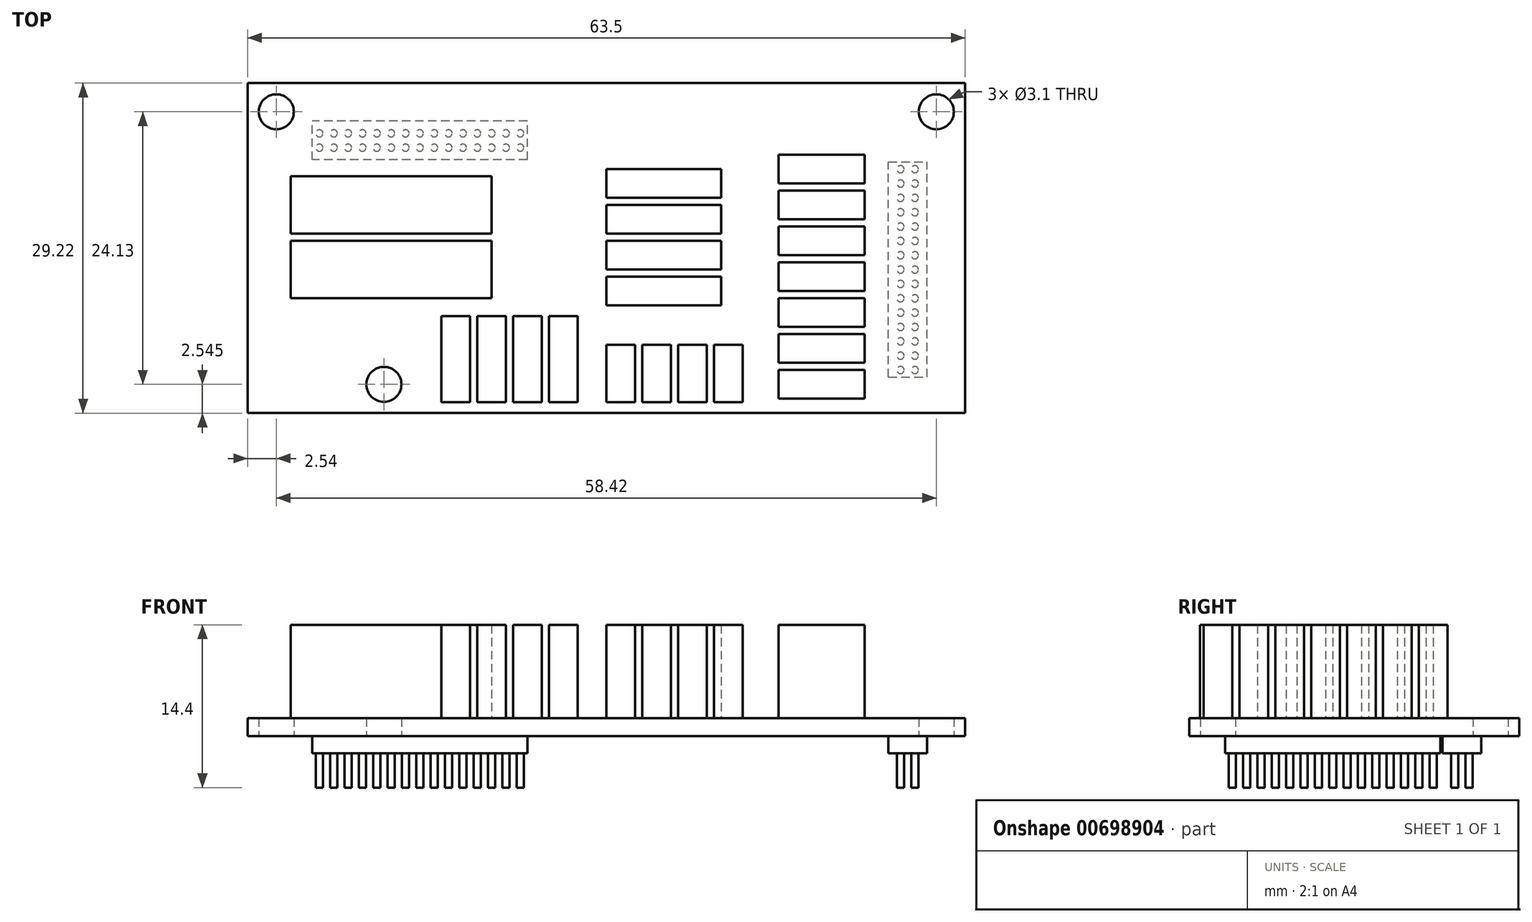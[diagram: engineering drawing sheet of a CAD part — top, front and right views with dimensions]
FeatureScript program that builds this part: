
annotation { "Feature Type Name" : "Feature", "Feature Type Description" : "" }
export const myFeature = defineFeature(function(context is Context, id is Id, definition is map)
    precondition{}
    {
        {
            var Q0;
            Q0=qCreatedBy(makeId("Top.planeOp"),FACE);
            var sketch = newSketch(context, id + "F0", { "sketchPlane" : qUnion([Q0])});
            skLineSegment(sketch, "E0.bottom", {"start": v(31.75, 14.6) * mm, "end": v(-31.75, 14.6) * mm});
            skLineSegment(sketch, "E0.top", {"start": v(31.75, -14.6) * mm, "end": v(-31.75, -14.6) * mm});
            skLineSegment(sketch, "E0.left", {"start": v(31.75, 14.6) * mm, "end": v(31.75, -14.6) * mm});
            skLineSegment(sketch, "E0.right", {"start": v(-31.75, 14.6) * mm, "end": v(-31.75, -14.6) * mm});
            skPoint(sketch, "E0.middle", {"position": v(0, 0) * mm});
            skCircle(sketch, "E1", {"center": v(-29.2, 12.07) * mm, "radius": 1.55 * mm});
            skCircle(sketch, "E2", {"center": v(29.21, 12.07) * mm, "radius": 1.55 * mm});
            skCircle(sketch, "E3", {"center": v(-19.69, -12.06) * mm, "radius": 1.55 * mm});
            skCircle(sketch, "E4", {"center": v(-25.4, 10.16) * mm, "radius": 0.32 * mm});
            skLineSegment(sketch, "E5", {"start": v(-29.2, 12.07) * mm, "end": v(29.21, 12.07) * mm, "construction": true});
            skCircle(sketch, "E6.1.0.0", {"center": v(-24.13, 10.16) * mm, "radius": 0.32 * mm});
            skCircle(sketch, "E6.2.0.0", {"center": v(-22.86, 10.16) * mm, "radius": 0.32 * mm});
            skCircle(sketch, "E6.3.0.0", {"center": v(-21.6, 10.16) * mm, "radius": 0.32 * mm});
            skCircle(sketch, "E6.4.0.0", {"center": v(-20.32, 10.16) * mm, "radius": 0.32 * mm});
            skCircle(sketch, "E6.5.0.0", {"center": v(-19.05, 10.16) * mm, "radius": 0.32 * mm});
            skCircle(sketch, "E6.6.0.0", {"center": v(-17.78, 10.16) * mm, "radius": 0.32 * mm});
            skCircle(sketch, "E6.7.0.0", {"center": v(-16.51, 10.16) * mm, "radius": 0.32 * mm});
            skCircle(sketch, "E6.8.0.0", {"center": v(-15.24, 10.16) * mm, "radius": 0.32 * mm});
            skCircle(sketch, "E6.9.0.0", {"center": v(-13.97, 10.16) * mm, "radius": 0.32 * mm});
            skCircle(sketch, "E6.10.0.0", {"center": v(-12.7, 10.16) * mm, "radius": 0.32 * mm});
            skCircle(sketch, "E6.11.0.0", {"center": v(-11.43, 10.16) * mm, "radius": 0.32 * mm});
            skCircle(sketch, "E6.12.0.0", {"center": v(-10.16, 10.16) * mm, "radius": 0.32 * mm});
            skCircle(sketch, "E6.13.0.0", {"center": v(-8.9, 10.16) * mm, "radius": 0.32 * mm});
            skCircle(sketch, "E6.14.0.0", {"center": v(-7.62, 10.16) * mm, "radius": 0.32 * mm});
            skLineSegment(sketch, "E6.direction1", {"start": v(-25.4, 10.16) * mm, "end": v(-24.13, 10.16) * mm, "construction": true});
            skCircle(sketch, "E7.1.0.0", {"center": v(-19.05, 8.89) * mm, "radius": 0.32 * mm});
            skCircle(sketch, "E7.1.0.1", {"center": v(-17.78, 8.89) * mm, "radius": 0.32 * mm});
            skCircle(sketch, "E7.1.0.2", {"center": v(-16.51, 8.89) * mm, "radius": 0.32 * mm});
            skCircle(sketch, "E7.1.0.3", {"center": v(-13.97, 8.89) * mm, "radius": 0.32 * mm});
            skCircle(sketch, "E7.1.0.4", {"center": v(-11.43, 8.89) * mm, "radius": 0.32 * mm});
            skCircle(sketch, "E7.1.0.5", {"center": v(-8.9, 8.89) * mm, "radius": 0.32 * mm});
            skCircle(sketch, "E7.1.0.6", {"center": v(-25.4, 8.9) * mm, "radius": 0.32 * mm});
            skCircle(sketch, "E7.1.0.7", {"center": v(-24.13, 8.9) * mm, "radius": 0.32 * mm});
            skCircle(sketch, "E7.1.0.8", {"center": v(-22.86, 8.89) * mm, "radius": 0.32 * mm});
            skCircle(sketch, "E7.1.0.9", {"center": v(-21.6, 8.89) * mm, "radius": 0.32 * mm});
            skCircle(sketch, "E7.1.0.10", {"center": v(-20.32, 8.89) * mm, "radius": 0.32 * mm});
            skLineSegment(sketch, "E7.1.0.11", {"start": v(-25.4, 8.9) * mm, "end": v(-24.13, 8.9) * mm, "construction": true});
            skCircle(sketch, "E7.1.0.12", {"center": v(-7.62, 8.89) * mm, "radius": 0.32 * mm});
            skCircle(sketch, "E7.1.0.13", {"center": v(-10.16, 8.89) * mm, "radius": 0.32 * mm});
            skCircle(sketch, "E7.1.0.14", {"center": v(-12.7, 8.89) * mm, "radius": 0.32 * mm});
            skCircle(sketch, "E7.1.0.15", {"center": v(-15.24, 8.89) * mm, "radius": 0.32 * mm});
            skLineSegment(sketch, "E7.direction1", {"start": v(-25.4, 10.16) * mm, "end": v(-25.4, 8.9) * mm, "construction": true});
            skCircle(sketch, "E8", {"center": v(-29.2, 12.07) * mm, "radius": 2.5 * mm, "construction": true});
            skCircle(sketch, "E9", {"center": v(27.3, 6.99) * mm, "radius": 0.32 * mm});
            skCircle(sketch, "E10.1.0.0", {"center": v(27.3, 5.72) * mm, "radius": 0.32 * mm});
            skCircle(sketch, "E10.2.0.0", {"center": v(27.3, 4.45) * mm, "radius": 0.32 * mm});
            skCircle(sketch, "E10.3.0.0", {"center": v(27.3, 3.18) * mm, "radius": 0.32 * mm});
            skCircle(sketch, "E10.4.0.0", {"center": v(27.3, 1.9) * mm, "radius": 0.32 * mm});
            skCircle(sketch, "E10.5.0.0", {"center": v(27.3, 0.64) * mm, "radius": 0.32 * mm});
            skCircle(sketch, "E10.6.0.0", {"center": v(27.3, -0.63) * mm, "radius": 0.32 * mm});
            skCircle(sketch, "E10.7.0.0", {"center": v(27.3, -1.9) * mm, "radius": 0.32 * mm});
            skCircle(sketch, "E10.8.0.0", {"center": v(27.3, -3.17) * mm, "radius": 0.32 * mm});
            skCircle(sketch, "E10.9.0.0", {"center": v(27.3, -4.44) * mm, "radius": 0.32 * mm});
            skCircle(sketch, "E10.10.0.0", {"center": v(27.3, -5.71) * mm, "radius": 0.32 * mm});
            skCircle(sketch, "E10.11.0.0", {"center": v(27.3, -6.98) * mm, "radius": 0.32 * mm});
            skCircle(sketch, "E10.12.0.0", {"center": v(27.3, -8.25) * mm, "radius": 0.32 * mm});
            skCircle(sketch, "E10.13.0.0", {"center": v(27.3, -9.52) * mm, "radius": 0.32 * mm});
            skCircle(sketch, "E10.14.0.0", {"center": v(27.3, -10.8) * mm, "radius": 0.32 * mm});
            skLineSegment(sketch, "E10.direction1", {"start": v(27.3, 6.99) * mm, "end": v(27.3, 5.72) * mm, "construction": true});
            skCircle(sketch, "E11.1.0.0", {"center": v(26.04, 0.64) * mm, "radius": 0.32 * mm});
            skCircle(sketch, "E11.1.0.1", {"center": v(26.04, -0.63) * mm, "radius": 0.32 * mm});
            skCircle(sketch, "E11.1.0.2", {"center": v(26.04, -1.9) * mm, "radius": 0.32 * mm});
            skCircle(sketch, "E11.1.0.3", {"center": v(26.04, -4.44) * mm, "radius": 0.32 * mm});
            skCircle(sketch, "E11.1.0.4", {"center": v(26.04, -6.98) * mm, "radius": 0.32 * mm});
            skCircle(sketch, "E11.1.0.5", {"center": v(26.04, -9.52) * mm, "radius": 0.32 * mm});
            skCircle(sketch, "E11.1.0.6", {"center": v(26.04, 6.99) * mm, "radius": 0.32 * mm});
            skCircle(sketch, "E11.1.0.7", {"center": v(26.04, 5.72) * mm, "radius": 0.32 * mm});
            skCircle(sketch, "E11.1.0.8", {"center": v(26.04, 4.45) * mm, "radius": 0.32 * mm});
            skCircle(sketch, "E11.1.0.9", {"center": v(26.04, 3.18) * mm, "radius": 0.32 * mm});
            skCircle(sketch, "E11.1.0.10", {"center": v(26.04, 1.9) * mm, "radius": 0.32 * mm});
            skLineSegment(sketch, "E11.1.0.11", {"start": v(26.04, 6.99) * mm, "end": v(26.04, 5.72) * mm, "construction": true});
            skCircle(sketch, "E11.1.0.12", {"center": v(26.04, -10.8) * mm, "radius": 0.32 * mm});
            skCircle(sketch, "E11.1.0.13", {"center": v(26.04, -8.25) * mm, "radius": 0.32 * mm});
            skCircle(sketch, "E11.1.0.14", {"center": v(26.04, -5.71) * mm, "radius": 0.32 * mm});
            skCircle(sketch, "E11.1.0.15", {"center": v(26.04, -3.17) * mm, "radius": 0.32 * mm});
            skLineSegment(sketch, "E11.direction1", {"start": v(27.3, 6.99) * mm, "end": v(26.04, 6.99) * mm, "construction": true});
            skLineSegment(sketch, "E12.bottom", {"start": v(-6.99, 7.81) * mm, "end": v(-26.04, 7.81) * mm});
            skLineSegment(sketch, "E12.top", {"start": v(-6.99, 11.24) * mm, "end": v(-26.04, 11.24) * mm});
            skLineSegment(sketch, "E12.left", {"start": v(-6.99, 7.81) * mm, "end": v(-6.99, 11.24) * mm});
            skLineSegment(sketch, "E12.right", {"start": v(-26.04, 7.81) * mm, "end": v(-26.04, 11.24) * mm});
            skPoint(sketch, "E12.middle", {"position": v(-16.51, 9.53) * mm});
            skLineSegment(sketch, "E13.bottom", {"start": v(24.96, -11.43) * mm, "end": v(28.39, -11.43) * mm});
            skLineSegment(sketch, "E13.top", {"start": v(24.96, 7.62) * mm, "end": v(28.39, 7.62) * mm});
            skLineSegment(sketch, "E13.left", {"start": v(24.96, -11.43) * mm, "end": v(24.96, 7.62) * mm});
            skLineSegment(sketch, "E13.right", {"start": v(28.39, -11.43) * mm, "end": v(28.39, 7.62) * mm});
            skPoint(sketch, "E13.middle", {"position": v(26.67, -1.9) * mm});
            skLineSegment(sketch, "E14", {"start": v(27.3, -1.9) * mm, "end": v(26.04, -1.9) * mm, "construction": true});
            skLineSegment(sketch, "E15", {"start": v(-16.51, 8.89) * mm, "end": v(-16.51, 10.16) * mm, "construction": true});
            skSolve(sketch);
        }
        {
            var Q0;
            Q0=makeQuery(id+"F0.imprint","IMPRINT",FACE,{"disambiguationData":[TD([[makeQuery(id+"F0.imprint","IMPRINT",EDGE,{"derivedFrom":sQuery(id+"F0.wireOp",EDGE,"E0.bottom")}),1.0]])]});
            var Q1;
            Q1=makeQuery(id+"F0.imprint","IMPRINT",FACE,{"disambiguationData":[TD([[makeQuery(id+"F0.imprint","IMPRINT",EDGE,{"derivedFrom":sQuery(id+"F0.wireOp",EDGE,"E7.1.0.1")}),1.0]])]});
            var Q2;
            Q2=makeQuery(id+"F0.imprint","IMPRINT",FACE,{"disambiguationData":[TD([[makeQuery(id+"F0.imprint","IMPRINT",EDGE,{"derivedFrom":sQuery(id+"F0.wireOp",EDGE,"E11.1.0.3")}),1.0]])]});
            var Q3;
            Q3=makeQuery(id+"F0.imprint","IMPRINT",FACE,{"disambiguationData":[TD([[makeQuery(id+"F0.imprint","IMPRINT",EDGE,{"derivedFrom":sQuery(id+"F0.wireOp",EDGE,"E10.2.0.0")}),1.0]])]});
            var Q4;
            Q4=makeQuery(id+"F0.imprint","IMPRINT",FACE,{"disambiguationData":[TD([[makeQuery(id+"F0.imprint","IMPRINT",EDGE,{"derivedFrom":sQuery(id+"F0.wireOp",EDGE,"E11.1.0.10")}),1.0]])]});
            var Q5;
            Q5=makeQuery(id+"F0.imprint","IMPRINT",FACE,{"disambiguationData":[TD([[makeQuery(id+"F0.imprint","IMPRINT",EDGE,{"derivedFrom":sQuery(id+"F0.wireOp",EDGE,"E10.9.0.0")}),1.0]])]});
            var Q6;
            Q6=makeQuery(id+"F0.imprint","IMPRINT",FACE,{"disambiguationData":[TD([[makeQuery(id+"F0.imprint","IMPRINT",EDGE,{"derivedFrom":sQuery(id+"F0.wireOp",EDGE,"E7.1.0.8")}),1.0]])]});
            var Q7;
            Q7=makeQuery(id+"F0.imprint","IMPRINT",FACE,{"disambiguationData":[TD([[makeQuery(id+"F0.imprint","IMPRINT",EDGE,{"derivedFrom":sQuery(id+"F0.wireOp",EDGE,"E7.1.0.2")}),1.0]])]});
            var Q8;
            Q8=makeQuery(id+"F0.imprint","IMPRINT",FACE,{"disambiguationData":[TD([[makeQuery(id+"F0.imprint","IMPRINT",EDGE,{"derivedFrom":sQuery(id+"F0.wireOp",EDGE,"E11.1.0.14")}),1.0]])]});
            var Q9;
            Q9=makeQuery(id+"F0.imprint","IMPRINT",FACE,{"disambiguationData":[TD([[makeQuery(id+"F0.imprint","IMPRINT",EDGE,{"derivedFrom":sQuery(id+"F0.wireOp",EDGE,"E10.12.0.0")}),1.0]])]});
            var Q10;
            Q10=makeQuery(id+"F0.imprint","IMPRINT",FACE,{"disambiguationData":[TD([[makeQuery(id+"F0.imprint","IMPRINT",EDGE,{"derivedFrom":sQuery(id+"F0.wireOp",EDGE,"E11.1.0.4")}),1.0]])]});
            var Q11;
            Q11=makeQuery(id+"F0.imprint","IMPRINT",FACE,{"disambiguationData":[TD([[makeQuery(id+"F0.imprint","IMPRINT",EDGE,{"derivedFrom":sQuery(id+"F0.wireOp",EDGE,"E7.1.0.12")}),1.0]])]});
            var Q12;
            Q12=makeQuery(id+"F0.imprint","IMPRINT",FACE,{"disambiguationData":[TD([[makeQuery(id+"F0.imprint","IMPRINT",EDGE,{"derivedFrom":sQuery(id+"F0.wireOp",EDGE,"E10.3.0.0")}),1.0]])]});
            var Q13;
            Q13=makeQuery(id+"F0.imprint","IMPRINT",FACE,{"disambiguationData":[TD([[makeQuery(id+"F0.imprint","IMPRINT",EDGE,{"derivedFrom":sQuery(id+"F0.wireOp",EDGE,"E11.1.0.12")}),1.0]])]});
            var Q14;
            Q14=makeQuery(id+"F0.imprint","IMPRINT",FACE,{"disambiguationData":[TD([[makeQuery(id+"F0.imprint","IMPRINT",EDGE,{"derivedFrom":sQuery(id+"F0.wireOp",EDGE,"E10.10.0.0")}),1.0]])]});
            var Q15;
            Q15=makeQuery(id+"F0.imprint","IMPRINT",FACE,{"disambiguationData":[TD([[makeQuery(id+"F0.imprint","IMPRINT",EDGE,{"derivedFrom":sQuery(id+"F0.wireOp",EDGE,"E7.1.0.9")}),1.0]])]});
            var Q16;
            Q16=makeQuery(id+"F0.imprint","IMPRINT",FACE,{"disambiguationData":[TD([[makeQuery(id+"F0.imprint","IMPRINT",EDGE,{"derivedFrom":sQuery(id+"F0.wireOp",EDGE,"E7.1.0.3")}),1.0]])]});
            var Q17;
            Q17=makeQuery(id+"F0.imprint","IMPRINT",FACE,{"disambiguationData":[TD([[makeQuery(id+"F0.imprint","IMPRINT",EDGE,{"derivedFrom":sQuery(id+"F0.wireOp",EDGE,"E11.1.0.15")}),1.0]])]});
            var Q18;
            Q18=makeQuery(id+"F0.imprint","IMPRINT",FACE,{"disambiguationData":[TD([[makeQuery(id+"F0.imprint","IMPRINT",EDGE,{"derivedFrom":sQuery(id+"F0.wireOp",EDGE,"E11.1.0.5")}),1.0]])]});
            var Q19;
            Q19=makeQuery(id+"F0.imprint","IMPRINT",FACE,{"disambiguationData":[TD([[makeQuery(id+"F0.imprint","IMPRINT",EDGE,{"derivedFrom":sQuery(id+"F0.wireOp",EDGE,"E10.13.0.0")}),1.0]])]});
            var Q20;
            Q20=makeQuery(id+"F0.imprint","IMPRINT",FACE,{"disambiguationData":[TD([[makeQuery(id+"F0.imprint","IMPRINT",EDGE,{"derivedFrom":sQuery(id+"F0.wireOp",EDGE,"E7.1.0.13")}),1.0]])]});
            var Q21;
            Q21=makeQuery(id+"F0.imprint","IMPRINT",FACE,{"disambiguationData":[TD([[makeQuery(id+"F0.imprint","IMPRINT",EDGE,{"derivedFrom":sQuery(id+"F0.wireOp",EDGE,"E10.4.0.0")}),1.0]])]});
            var Q22;
            Q22=makeQuery(id+"F0.imprint","IMPRINT",FACE,{"disambiguationData":[TD([[makeQuery(id+"F0.imprint","IMPRINT",EDGE,{"derivedFrom":sQuery(id+"F0.wireOp",EDGE,"E11.1.0.13")}),1.0]])]});
            var Q23;
            Q23=makeQuery(id+"F0.imprint","IMPRINT",FACE,{"disambiguationData":[TD([[makeQuery(id+"F0.imprint","IMPRINT",EDGE,{"derivedFrom":sQuery(id+"F0.wireOp",EDGE,"E10.11.0.0")}),1.0]])]});
            var Q24;
            Q24=makeQuery(id+"F0.imprint","IMPRINT",FACE,{"disambiguationData":[TD([[makeQuery(id+"F0.imprint","IMPRINT",EDGE,{"derivedFrom":sQuery(id+"F0.wireOp",EDGE,"E7.1.0.10")}),1.0]])]});
            var Q25;
            Q25=makeQuery(id+"F0.imprint","IMPRINT",FACE,{"disambiguationData":[TD([[makeQuery(id+"F0.imprint","IMPRINT",EDGE,{"derivedFrom":sQuery(id+"F0.wireOp",EDGE,"E11.1.0.6")}),1.0]])]});
            var Q26;
            Q26=makeQuery(id+"F0.imprint","IMPRINT",FACE,{"disambiguationData":[TD([[makeQuery(id+"F0.imprint","IMPRINT",EDGE,{"derivedFrom":sQuery(id+"F0.wireOp",EDGE,"E10.5.0.0")}),1.0]])]});
            var Q27;
            Q27=makeQuery(id+"F0.imprint","IMPRINT",FACE,{"disambiguationData":[TD([[makeQuery(id+"F0.imprint","IMPRINT",EDGE,{"derivedFrom":sQuery(id+"F0.wireOp",EDGE,"E7.1.0.4")}),1.0]])]});
            var Q28;
            Q28=makeQuery(id+"F0.imprint","IMPRINT",FACE,{"disambiguationData":[TD([[makeQuery(id+"F0.imprint","IMPRINT",EDGE,{"derivedFrom":sQuery(id+"F0.wireOp",EDGE,"E6.12.0.0")}),1.0]])]});
            var Q29;
            Q29=makeQuery(id+"F0.imprint","IMPRINT",FACE,{"disambiguationData":[TD([[makeQuery(id+"F0.imprint","IMPRINT",EDGE,{"derivedFrom":sQuery(id+"F0.wireOp",EDGE,"E6.10.0.0")}),1.0]])]});
            var Q30;
            Q30=makeQuery(id+"F0.imprint","IMPRINT",FACE,{"disambiguationData":[TD([[makeQuery(id+"F0.imprint","IMPRINT",EDGE,{"derivedFrom":sQuery(id+"F0.wireOp",EDGE,"E6.11.0.0")}),1.0]])]});
            var Q31;
            Q31=makeQuery(id+"F0.imprint","IMPRINT",FACE,{"disambiguationData":[TD([[makeQuery(id+"F0.imprint","IMPRINT",EDGE,{"derivedFrom":sQuery(id+"F0.wireOp",EDGE,"E6.13.0.0")}),1.0]])]});
            var Q32;
            Q32=makeQuery(id+"F0.imprint","IMPRINT",FACE,{"disambiguationData":[TD([[makeQuery(id+"F0.imprint","IMPRINT",EDGE,{"derivedFrom":sQuery(id+"F0.wireOp",EDGE,"E11.1.0.0")}),1.0]])]});
            var Q33;
            Q33=makeQuery(id+"F0.imprint","IMPRINT",FACE,{"disambiguationData":[TD([[makeQuery(id+"F0.imprint","IMPRINT",EDGE,{"derivedFrom":sQuery(id+"F0.wireOp",EDGE,"E7.1.0.15")}),1.0]])]});
            var Q34;
            Q34=makeQuery(id+"F0.imprint","IMPRINT",FACE,{"disambiguationData":[TD([[makeQuery(id+"F0.imprint","IMPRINT",EDGE,{"derivedFrom":sQuery(id+"F0.wireOp",EDGE,"E4")}),1.0]])]});
            var Q35;
            Q35=makeQuery(id+"F0.imprint","IMPRINT",FACE,{"disambiguationData":[TD([[makeQuery(id+"F0.imprint","IMPRINT",EDGE,{"derivedFrom":sQuery(id+"F0.wireOp",EDGE,"E6.1.0.0")}),1.0]])]});
            var Q36;
            Q36=makeQuery(id+"F0.imprint","IMPRINT",FACE,{"disambiguationData":[TD([[makeQuery(id+"F0.imprint","IMPRINT",EDGE,{"derivedFrom":sQuery(id+"F0.wireOp",EDGE,"E6.2.0.0")}),1.0]])]});
            var Q37;
            Q37=makeQuery(id+"F0.imprint","IMPRINT",FACE,{"disambiguationData":[TD([[makeQuery(id+"F0.imprint","IMPRINT",EDGE,{"derivedFrom":sQuery(id+"F0.wireOp",EDGE,"E6.3.0.0")}),1.0]])]});
            var Q38;
            Q38=makeQuery(id+"F0.imprint","IMPRINT",FACE,{"disambiguationData":[TD([[makeQuery(id+"F0.imprint","IMPRINT",EDGE,{"derivedFrom":sQuery(id+"F0.wireOp",EDGE,"E6.4.0.0")}),1.0]])]});
            var Q39;
            Q39=makeQuery(id+"F0.imprint","IMPRINT",FACE,{"disambiguationData":[TD([[makeQuery(id+"F0.imprint","IMPRINT",EDGE,{"derivedFrom":sQuery(id+"F0.wireOp",EDGE,"E6.5.0.0")}),1.0]])]});
            var Q40;
            Q40=makeQuery(id+"F0.imprint","IMPRINT",FACE,{"disambiguationData":[TD([[makeQuery(id+"F0.imprint","IMPRINT",EDGE,{"derivedFrom":sQuery(id+"F0.wireOp",EDGE,"E6.6.0.0")}),1.0]])]});
            var Q41;
            Q41=makeQuery(id+"F0.imprint","IMPRINT",FACE,{"disambiguationData":[TD([[makeQuery(id+"F0.imprint","IMPRINT",EDGE,{"derivedFrom":sQuery(id+"F0.wireOp",EDGE,"E6.7.0.0")}),1.0]])]});
            var Q42;
            Q42=makeQuery(id+"F0.imprint","IMPRINT",FACE,{"disambiguationData":[TD([[makeQuery(id+"F0.imprint","IMPRINT",EDGE,{"derivedFrom":sQuery(id+"F0.wireOp",EDGE,"E6.8.0.0")}),1.0]])]});
            var Q43;
            Q43=makeQuery(id+"F0.imprint","IMPRINT",FACE,{"disambiguationData":[TD([[makeQuery(id+"F0.imprint","IMPRINT",EDGE,{"derivedFrom":sQuery(id+"F0.wireOp",EDGE,"E6.9.0.0")}),1.0]])]});
            var Q44;
            Q44=makeQuery(id+"F0.imprint","IMPRINT",FACE,{"disambiguationData":[TD([[makeQuery(id+"F0.imprint","IMPRINT",EDGE,{"derivedFrom":sQuery(id+"F0.wireOp",EDGE,"E11.1.0.7")}),1.0]])]});
            var Q45;
            Q45=makeQuery(id+"F0.imprint","IMPRINT",FACE,{"disambiguationData":[TD([[makeQuery(id+"F0.imprint","IMPRINT",EDGE,{"derivedFrom":sQuery(id+"F0.wireOp",EDGE,"E10.6.0.0")}),1.0]])]});
            var Q46;
            Q46=makeQuery(id+"F0.imprint","IMPRINT",FACE,{"disambiguationData":[TD([[makeQuery(id+"F0.imprint","IMPRINT",EDGE,{"derivedFrom":sQuery(id+"F0.wireOp",EDGE,"E7.1.0.5")}),1.0]])]});
            var Q47;
            Q47=makeQuery(id+"F0.imprint","IMPRINT",FACE,{"disambiguationData":[TD([[makeQuery(id+"F0.imprint","IMPRINT",EDGE,{"derivedFrom":sQuery(id+"F0.wireOp",EDGE,"E6.14.0.0")}),1.0]])]});
            var Q48;
            Q48=makeQuery(id+"F0.imprint","IMPRINT",FACE,{"disambiguationData":[TD([[makeQuery(id+"F0.imprint","IMPRINT",EDGE,{"derivedFrom":sQuery(id+"F0.wireOp",EDGE,"E11.1.0.1")}),1.0]])]});
            var Q49;
            Q49=makeQuery(id+"F0.imprint","IMPRINT",FACE,{"disambiguationData":[TD([[makeQuery(id+"F0.imprint","IMPRINT",EDGE,{"derivedFrom":sQuery(id+"F0.wireOp",EDGE,"E9")}),1.0]])]});
            var Q50;
            Q50=makeQuery(id+"F0.imprint","IMPRINT",FACE,{"disambiguationData":[TD([[makeQuery(id+"F0.imprint","IMPRINT",EDGE,{"derivedFrom":sQuery(id+"F0.wireOp",EDGE,"E11.1.0.8")}),1.0]])]});
            var Q51;
            Q51=makeQuery(id+"F0.imprint","IMPRINT",FACE,{"disambiguationData":[TD([[makeQuery(id+"F0.imprint","IMPRINT",EDGE,{"derivedFrom":sQuery(id+"F0.wireOp",EDGE,"E10.7.0.0")}),1.0]])]});
            var Q52;
            Q52=makeQuery(id+"F0.imprint","IMPRINT",FACE,{"disambiguationData":[TD([[makeQuery(id+"F0.imprint","IMPRINT",EDGE,{"derivedFrom":sQuery(id+"F0.wireOp",EDGE,"E7.1.0.6")}),1.0]])]});
            var Q53;
            Q53=makeQuery(id+"F0.imprint","IMPRINT",FACE,{"disambiguationData":[TD([[makeQuery(id+"F0.imprint","IMPRINT",EDGE,{"derivedFrom":sQuery(id+"F0.wireOp",EDGE,"E7.1.0.0")}),1.0]])]});
            var Q54;
            Q54=makeQuery(id+"F0.imprint","IMPRINT",FACE,{"disambiguationData":[TD([[makeQuery(id+"F0.imprint","IMPRINT",EDGE,{"derivedFrom":sQuery(id+"F0.wireOp",EDGE,"E11.1.0.2")}),1.0]])]});
            var Q55;
            Q55=makeQuery(id+"F0.imprint","IMPRINT",FACE,{"disambiguationData":[TD([[makeQuery(id+"F0.imprint","IMPRINT",EDGE,{"derivedFrom":sQuery(id+"F0.wireOp",EDGE,"E10.1.0.0")}),1.0]])]});
            var Q56;
            Q56=makeQuery(id+"F0.imprint","IMPRINT",FACE,{"disambiguationData":[TD([[makeQuery(id+"F0.imprint","IMPRINT",EDGE,{"derivedFrom":sQuery(id+"F0.wireOp",EDGE,"E7.1.0.14")}),1.0]])]});
            var Q57;
            Q57=makeQuery(id+"F0.imprint","IMPRINT",FACE,{"disambiguationData":[TD([[makeQuery(id+"F0.imprint","IMPRINT",EDGE,{"derivedFrom":sQuery(id+"F0.wireOp",EDGE,"E11.1.0.9")}),1.0]])]});
            var Q58;
            Q58=makeQuery(id+"F0.imprint","IMPRINT",FACE,{"disambiguationData":[TD([[makeQuery(id+"F0.imprint","IMPRINT",EDGE,{"derivedFrom":sQuery(id+"F0.wireOp",EDGE,"E10.8.0.0")}),1.0]])]});
            var Q59;
            Q59=makeQuery(id+"F0.imprint","IMPRINT",FACE,{"disambiguationData":[TD([[makeQuery(id+"F0.imprint","IMPRINT",EDGE,{"derivedFrom":sQuery(id+"F0.wireOp",EDGE,"E7.1.0.7")}),1.0]])]});
            var Q60;
            Q60=makeQuery(id+"F0.imprint","IMPRINT",FACE,{"disambiguationData":[TD([[makeQuery(id+"F0.imprint","IMPRINT",EDGE,{"derivedFrom":sQuery(id+"F0.wireOp",EDGE,"E10.14.0.0")}),1.0]])]});
            var Q61;
            Q61=makeQuery(id+"F0.imprint","IMPRINT",FACE,{"disambiguationData":[TD([[makeQuery(id+"F0.imprint","IMPRINT",EDGE,{"derivedFrom":sQuery(id+"F0.wireOp",EDGE,"E4")}),-1.0]])]});
            var Q62;
            Q62=makeQuery(id+"F0.imprint","IMPRINT",FACE,{"disambiguationData":[TD([[makeQuery(id+"F0.imprint","IMPRINT",EDGE,{"derivedFrom":sQuery(id+"F0.wireOp",EDGE,"E9")}),-1.0]])]});
            extrude(context, id + "F1", {"entities" : qUnion([Q0, Q1, Q2, Q3, Q4, Q5, Q6, Q7, Q8, Q9, Q10, Q11, Q12, Q13, Q14, Q15, Q16, Q17, Q18, Q19, Q20, Q21, Q22, Q23, Q24, Q25, Q26, Q27, Q28, Q29, Q30, Q31, Q32, Q33, Q34, Q35, Q36, Q37, Q38, Q39, Q40, Q41, Q42, Q43, Q44, Q45, Q46, Q47, Q48, Q49, Q50, Q51, Q52, Q53, Q54, Q55, Q56, Q57, Q58, Q59, Q60, Q61, Q62]), "depth" : 1.6 * mm});
        }
        {
            var Q0;
            Q0=makeQuery(id+"F0.imprint","IMPRINT",FACE,{"disambiguationData":[TD([[makeQuery(id+"F0.imprint","IMPRINT",EDGE,{"derivedFrom":sQuery(id+"F0.wireOp",EDGE,"E7.1.0.5")}),1.0]])]});
            var Q1;
            Q1=makeQuery(id+"F0.imprint","IMPRINT",FACE,{"disambiguationData":[TD([[makeQuery(id+"F0.imprint","IMPRINT",EDGE,{"derivedFrom":sQuery(id+"F0.wireOp",EDGE,"E7.1.0.14")}),1.0]])]});
            var Q2;
            Q2=makeQuery(id+"F0.imprint","IMPRINT",FACE,{"disambiguationData":[TD([[makeQuery(id+"F0.imprint","IMPRINT",EDGE,{"derivedFrom":sQuery(id+"F0.wireOp",EDGE,"E7.1.0.7")}),1.0]])]});
            var Q3;
            Q3=makeQuery(id+"F0.imprint","IMPRINT",FACE,{"disambiguationData":[TD([[makeQuery(id+"F0.imprint","IMPRINT",EDGE,{"derivedFrom":sQuery(id+"F0.wireOp",EDGE,"E6.9.0.0")}),1.0]])]});
            var Q4;
            Q4=makeQuery(id+"F0.imprint","IMPRINT",FACE,{"disambiguationData":[TD([[makeQuery(id+"F0.imprint","IMPRINT",EDGE,{"derivedFrom":sQuery(id+"F0.wireOp",EDGE,"E6.8.0.0")}),1.0]])]});
            var Q5;
            Q5=makeQuery(id+"F0.imprint","IMPRINT",FACE,{"disambiguationData":[TD([[makeQuery(id+"F0.imprint","IMPRINT",EDGE,{"derivedFrom":sQuery(id+"F0.wireOp",EDGE,"E6.7.0.0")}),1.0]])]});
            var Q6;
            Q6=makeQuery(id+"F0.imprint","IMPRINT",FACE,{"disambiguationData":[TD([[makeQuery(id+"F0.imprint","IMPRINT",EDGE,{"derivedFrom":sQuery(id+"F0.wireOp",EDGE,"E6.6.0.0")}),1.0]])]});
            var Q7;
            Q7=makeQuery(id+"F0.imprint","IMPRINT",FACE,{"disambiguationData":[TD([[makeQuery(id+"F0.imprint","IMPRINT",EDGE,{"derivedFrom":sQuery(id+"F0.wireOp",EDGE,"E6.5.0.0")}),1.0]])]});
            var Q8;
            Q8=makeQuery(id+"F0.imprint","IMPRINT",FACE,{"disambiguationData":[TD([[makeQuery(id+"F0.imprint","IMPRINT",EDGE,{"derivedFrom":sQuery(id+"F0.wireOp",EDGE,"E6.4.0.0")}),1.0]])]});
            var Q9;
            Q9=makeQuery(id+"F0.imprint","IMPRINT",FACE,{"disambiguationData":[TD([[makeQuery(id+"F0.imprint","IMPRINT",EDGE,{"derivedFrom":sQuery(id+"F0.wireOp",EDGE,"E6.3.0.0")}),1.0]])]});
            var Q10;
            Q10=makeQuery(id+"F0.imprint","IMPRINT",FACE,{"disambiguationData":[TD([[makeQuery(id+"F0.imprint","IMPRINT",EDGE,{"derivedFrom":sQuery(id+"F0.wireOp",EDGE,"E7.1.0.2")}),1.0]])]});
            var Q11;
            Q11=makeQuery(id+"F0.imprint","IMPRINT",FACE,{"disambiguationData":[TD([[makeQuery(id+"F0.imprint","IMPRINT",EDGE,{"derivedFrom":sQuery(id+"F0.wireOp",EDGE,"E6.2.0.0")}),1.0]])]});
            var Q12;
            Q12=makeQuery(id+"F0.imprint","IMPRINT",FACE,{"disambiguationData":[TD([[makeQuery(id+"F0.imprint","IMPRINT",EDGE,{"derivedFrom":sQuery(id+"F0.wireOp",EDGE,"E6.1.0.0")}),1.0]])]});
            var Q13;
            Q13=makeQuery(id+"F0.imprint","IMPRINT",FACE,{"disambiguationData":[TD([[makeQuery(id+"F0.imprint","IMPRINT",EDGE,{"derivedFrom":sQuery(id+"F0.wireOp",EDGE,"E4")}),1.0]])]});
            var Q14;
            Q14=makeQuery(id+"F0.imprint","IMPRINT",FACE,{"disambiguationData":[TD([[makeQuery(id+"F0.imprint","IMPRINT",EDGE,{"derivedFrom":sQuery(id+"F0.wireOp",EDGE,"E7.1.0.1")}),1.0]])]});
            var Q15;
            Q15=makeQuery(id+"F0.imprint","IMPRINT",FACE,{"disambiguationData":[TD([[makeQuery(id+"F0.imprint","IMPRINT",EDGE,{"derivedFrom":sQuery(id+"F0.wireOp",EDGE,"E7.1.0.0")}),1.0]])]});
            var Q16;
            Q16=makeQuery(id+"F0.imprint","IMPRINT",FACE,{"disambiguationData":[TD([[makeQuery(id+"F0.imprint","IMPRINT",EDGE,{"derivedFrom":sQuery(id+"F0.wireOp",EDGE,"E6.11.0.0")}),1.0]])]});
            var Q17;
            Q17=makeQuery(id+"F0.imprint","IMPRINT",FACE,{"disambiguationData":[TD([[makeQuery(id+"F0.imprint","IMPRINT",EDGE,{"derivedFrom":sQuery(id+"F0.wireOp",EDGE,"E6.10.0.0")}),1.0]])]});
            var Q18;
            Q18=makeQuery(id+"F0.imprint","IMPRINT",FACE,{"disambiguationData":[TD([[makeQuery(id+"F0.imprint","IMPRINT",EDGE,{"derivedFrom":sQuery(id+"F0.wireOp",EDGE,"E6.12.0.0")}),1.0]])]});
            var Q19;
            Q19=makeQuery(id+"F0.imprint","IMPRINT",FACE,{"disambiguationData":[TD([[makeQuery(id+"F0.imprint","IMPRINT",EDGE,{"derivedFrom":sQuery(id+"F0.wireOp",EDGE,"E6.14.0.0")}),1.0]])]});
            var Q20;
            Q20=makeQuery(id+"F0.imprint","IMPRINT",FACE,{"disambiguationData":[TD([[makeQuery(id+"F0.imprint","IMPRINT",EDGE,{"derivedFrom":sQuery(id+"F0.wireOp",EDGE,"E7.1.0.4")}),1.0]])]});
            var Q21;
            Q21=makeQuery(id+"F0.imprint","IMPRINT",FACE,{"disambiguationData":[TD([[makeQuery(id+"F0.imprint","IMPRINT",EDGE,{"derivedFrom":sQuery(id+"F0.wireOp",EDGE,"E7.1.0.15")}),1.0]])]});
            var Q22;
            Q22=makeQuery(id+"F0.imprint","IMPRINT",FACE,{"disambiguationData":[TD([[makeQuery(id+"F0.imprint","IMPRINT",EDGE,{"derivedFrom":sQuery(id+"F0.wireOp",EDGE,"E6.13.0.0")}),1.0]])]});
            var Q23;
            Q23=makeQuery(id+"F0.imprint","IMPRINT",FACE,{"disambiguationData":[TD([[makeQuery(id+"F0.imprint","IMPRINT",EDGE,{"derivedFrom":sQuery(id+"F0.wireOp",EDGE,"E7.1.0.10")}),1.0]])]});
            var Q24;
            Q24=makeQuery(id+"F0.imprint","IMPRINT",FACE,{"disambiguationData":[TD([[makeQuery(id+"F0.imprint","IMPRINT",EDGE,{"derivedFrom":sQuery(id+"F0.wireOp",EDGE,"E7.1.0.13")}),1.0]])]});
            var Q25;
            Q25=makeQuery(id+"F0.imprint","IMPRINT",FACE,{"disambiguationData":[TD([[makeQuery(id+"F0.imprint","IMPRINT",EDGE,{"derivedFrom":sQuery(id+"F0.wireOp",EDGE,"E7.1.0.9")}),1.0]])]});
            var Q26;
            Q26=makeQuery(id+"F0.imprint","IMPRINT",FACE,{"disambiguationData":[TD([[makeQuery(id+"F0.imprint","IMPRINT",EDGE,{"derivedFrom":sQuery(id+"F0.wireOp",EDGE,"E7.1.0.12")}),1.0]])]});
            var Q27;
            Q27=makeQuery(id+"F0.imprint","IMPRINT",FACE,{"disambiguationData":[TD([[makeQuery(id+"F0.imprint","IMPRINT",EDGE,{"derivedFrom":sQuery(id+"F0.wireOp",EDGE,"E7.1.0.8")}),1.0]])]});
            var Q28;
            Q28=makeQuery(id+"F0.imprint","IMPRINT",FACE,{"disambiguationData":[TD([[makeQuery(id+"F0.imprint","IMPRINT",EDGE,{"derivedFrom":sQuery(id+"F0.wireOp",EDGE,"E7.1.0.3")}),1.0]])]});
            var Q29;
            Q29=makeQuery(id+"F0.imprint","IMPRINT",FACE,{"disambiguationData":[TD([[makeQuery(id+"F0.imprint","IMPRINT",EDGE,{"derivedFrom":sQuery(id+"F0.wireOp",EDGE,"E10.8.0.0")}),1.0]])]});
            var Q30;
            Q30=makeQuery(id+"F0.imprint","IMPRINT",FACE,{"disambiguationData":[TD([[makeQuery(id+"F0.imprint","IMPRINT",EDGE,{"derivedFrom":sQuery(id+"F0.wireOp",EDGE,"E11.1.0.9")}),1.0]])]});
            var Q31;
            Q31=makeQuery(id+"F0.imprint","IMPRINT",FACE,{"disambiguationData":[TD([[makeQuery(id+"F0.imprint","IMPRINT",EDGE,{"derivedFrom":sQuery(id+"F0.wireOp",EDGE,"E11.1.0.7")}),1.0]])]});
            var Q32;
            Q32=makeQuery(id+"F0.imprint","IMPRINT",FACE,{"disambiguationData":[TD([[makeQuery(id+"F0.imprint","IMPRINT",EDGE,{"derivedFrom":sQuery(id+"F0.wireOp",EDGE,"E10.6.0.0")}),1.0]])]});
            var Q33;
            Q33=makeQuery(id+"F0.imprint","IMPRINT",FACE,{"disambiguationData":[TD([[makeQuery(id+"F0.imprint","IMPRINT",EDGE,{"derivedFrom":sQuery(id+"F0.wireOp",EDGE,"E11.1.0.8")}),1.0]])]});
            var Q34;
            Q34=makeQuery(id+"F0.imprint","IMPRINT",FACE,{"disambiguationData":[TD([[makeQuery(id+"F0.imprint","IMPRINT",EDGE,{"derivedFrom":sQuery(id+"F0.wireOp",EDGE,"E10.7.0.0")}),1.0]])]});
            var Q35;
            Q35=makeQuery(id+"F0.imprint","IMPRINT",FACE,{"disambiguationData":[TD([[makeQuery(id+"F0.imprint","IMPRINT",EDGE,{"derivedFrom":sQuery(id+"F0.wireOp",EDGE,"E11.1.0.4")}),1.0]])]});
            var Q36;
            Q36=makeQuery(id+"F0.imprint","IMPRINT",FACE,{"disambiguationData":[TD([[makeQuery(id+"F0.imprint","IMPRINT",EDGE,{"derivedFrom":sQuery(id+"F0.wireOp",EDGE,"E10.3.0.0")}),1.0]])]});
            var Q37;
            Q37=makeQuery(id+"F0.imprint","IMPRINT",FACE,{"disambiguationData":[TD([[makeQuery(id+"F0.imprint","IMPRINT",EDGE,{"derivedFrom":sQuery(id+"F0.wireOp",EDGE,"E10.2.0.0")}),1.0]])]});
            var Q38;
            Q38=makeQuery(id+"F0.imprint","IMPRINT",FACE,{"disambiguationData":[TD([[makeQuery(id+"F0.imprint","IMPRINT",EDGE,{"derivedFrom":sQuery(id+"F0.wireOp",EDGE,"E11.1.0.3")}),1.0]])]});
            var Q39;
            Q39=makeQuery(id+"F0.imprint","IMPRINT",FACE,{"disambiguationData":[TD([[makeQuery(id+"F0.imprint","IMPRINT",EDGE,{"derivedFrom":sQuery(id+"F0.wireOp",EDGE,"E10.1.0.0")}),1.0]])]});
            var Q40;
            Q40=makeQuery(id+"F0.imprint","IMPRINT",FACE,{"disambiguationData":[TD([[makeQuery(id+"F0.imprint","IMPRINT",EDGE,{"derivedFrom":sQuery(id+"F0.wireOp",EDGE,"E11.1.0.2")}),1.0]])]});
            var Q41;
            Q41=makeQuery(id+"F0.imprint","IMPRINT",FACE,{"disambiguationData":[TD([[makeQuery(id+"F0.imprint","IMPRINT",EDGE,{"derivedFrom":sQuery(id+"F0.wireOp",EDGE,"E9")}),1.0]])]});
            var Q42;
            Q42=makeQuery(id+"F0.imprint","IMPRINT",FACE,{"disambiguationData":[TD([[makeQuery(id+"F0.imprint","IMPRINT",EDGE,{"derivedFrom":sQuery(id+"F0.wireOp",EDGE,"E11.1.0.1")}),1.0]])]});
            var Q43;
            Q43=makeQuery(id+"F0.imprint","IMPRINT",FACE,{"disambiguationData":[TD([[makeQuery(id+"F0.imprint","IMPRINT",EDGE,{"derivedFrom":sQuery(id+"F0.wireOp",EDGE,"E10.5.0.0")}),1.0]])]});
            var Q44;
            Q44=makeQuery(id+"F0.imprint","IMPRINT",FACE,{"disambiguationData":[TD([[makeQuery(id+"F0.imprint","IMPRINT",EDGE,{"derivedFrom":sQuery(id+"F0.wireOp",EDGE,"E11.1.0.6")}),1.0]])]});
            var Q45;
            Q45=makeQuery(id+"F0.imprint","IMPRINT",FACE,{"disambiguationData":[TD([[makeQuery(id+"F0.imprint","IMPRINT",EDGE,{"derivedFrom":sQuery(id+"F0.wireOp",EDGE,"E11.1.0.0")}),1.0]])]});
            var Q46;
            Q46=makeQuery(id+"F0.imprint","IMPRINT",FACE,{"disambiguationData":[TD([[makeQuery(id+"F0.imprint","IMPRINT",EDGE,{"derivedFrom":sQuery(id+"F0.wireOp",EDGE,"E10.11.0.0")}),1.0]])]});
            var Q47;
            Q47=makeQuery(id+"F0.imprint","IMPRINT",FACE,{"disambiguationData":[TD([[makeQuery(id+"F0.imprint","IMPRINT",EDGE,{"derivedFrom":sQuery(id+"F0.wireOp",EDGE,"E11.1.0.13")}),1.0]])]});
            var Q48;
            Q48=makeQuery(id+"F0.imprint","IMPRINT",FACE,{"disambiguationData":[TD([[makeQuery(id+"F0.imprint","IMPRINT",EDGE,{"derivedFrom":sQuery(id+"F0.wireOp",EDGE,"E10.13.0.0")}),1.0]])]});
            var Q49;
            Q49=makeQuery(id+"F0.imprint","IMPRINT",FACE,{"disambiguationData":[TD([[makeQuery(id+"F0.imprint","IMPRINT",EDGE,{"derivedFrom":sQuery(id+"F0.wireOp",EDGE,"E11.1.0.15")}),1.0]])]});
            var Q50;
            Q50=makeQuery(id+"F0.imprint","IMPRINT",FACE,{"disambiguationData":[TD([[makeQuery(id+"F0.imprint","IMPRINT",EDGE,{"derivedFrom":sQuery(id+"F0.wireOp",EDGE,"E10.10.0.0")}),1.0]])]});
            var Q51;
            Q51=makeQuery(id+"F0.imprint","IMPRINT",FACE,{"disambiguationData":[TD([[makeQuery(id+"F0.imprint","IMPRINT",EDGE,{"derivedFrom":sQuery(id+"F0.wireOp",EDGE,"E11.1.0.12")}),1.0]])]});
            var Q52;
            Q52=makeQuery(id+"F0.imprint","IMPRINT",FACE,{"disambiguationData":[TD([[makeQuery(id+"F0.imprint","IMPRINT",EDGE,{"derivedFrom":sQuery(id+"F0.wireOp",EDGE,"E10.12.0.0")}),1.0]])]});
            var Q53;
            Q53=makeQuery(id+"F0.imprint","IMPRINT",FACE,{"disambiguationData":[TD([[makeQuery(id+"F0.imprint","IMPRINT",EDGE,{"derivedFrom":sQuery(id+"F0.wireOp",EDGE,"E11.1.0.14")}),1.0]])]});
            var Q54;
            Q54=makeQuery(id+"F0.imprint","IMPRINT",FACE,{"disambiguationData":[TD([[makeQuery(id+"F0.imprint","IMPRINT",EDGE,{"derivedFrom":sQuery(id+"F0.wireOp",EDGE,"E10.9.0.0")}),1.0]])]});
            var Q55;
            Q55=makeQuery(id+"F0.imprint","IMPRINT",FACE,{"disambiguationData":[TD([[makeQuery(id+"F0.imprint","IMPRINT",EDGE,{"derivedFrom":sQuery(id+"F0.wireOp",EDGE,"E11.1.0.10")}),1.0]])]});
            var Q56;
            Q56=makeQuery(id+"F0.imprint","IMPRINT",FACE,{"disambiguationData":[TD([[makeQuery(id+"F0.imprint","IMPRINT",EDGE,{"derivedFrom":sQuery(id+"F0.wireOp",EDGE,"E10.4.0.0")}),1.0]])]});
            var Q57;
            Q57=makeQuery(id+"F0.imprint","IMPRINT",FACE,{"disambiguationData":[TD([[makeQuery(id+"F0.imprint","IMPRINT",EDGE,{"derivedFrom":sQuery(id+"F0.wireOp",EDGE,"E11.1.0.5")}),1.0]])]});
            var Q58;
            Q58=makeQuery(id+"F0.imprint","IMPRINT",FACE,{"disambiguationData":[TD([[makeQuery(id+"F0.imprint","IMPRINT",EDGE,{"derivedFrom":sQuery(id+"F0.wireOp",EDGE,"E10.14.0.0")}),1.0]])]});
            var Q59;
            Q59=makeQuery(id+"F0.imprint","IMPRINT",FACE,{"disambiguationData":[TD([[makeQuery(id+"F0.imprint","IMPRINT",EDGE,{"derivedFrom":sQuery(id+"F0.wireOp",EDGE,"E7.1.0.6")}),1.0]])]});
            extrude(context, id + "F2", {"entities" : qUnion([Q0, Q1, Q2, Q3, Q4, Q5, Q6, Q7, Q8, Q9, Q10, Q11, Q12, Q13, Q14, Q15, Q16, Q17, Q18, Q19, Q20, Q21, Q22, Q23, Q24, Q25, Q26, Q27, Q28, Q29, Q30, Q31, Q32, Q33, Q34, Q35, Q36, Q37, Q38, Q39, Q40, Q41, Q42, Q43, Q44, Q45, Q46, Q47, Q48, Q49, Q50, Q51, Q52, Q53, Q54, Q55, Q56, Q57, Q58, Q59]), "operationType" : NewBodyOperationType.ADD, "oppositeDirection" : true, "depth" : 1.5 * mm + 3.05 * mm});
        }
        {
            var Q0;
            Q0=makeQuery(id+"F0.imprint","IMPRINT",FACE,{"disambiguationData":[TD([[makeQuery(id+"F0.imprint","IMPRINT",EDGE,{"derivedFrom":sQuery(id+"F0.wireOp",EDGE,"E9")}),-1.0]])]});
            var Q1;
            Q1=makeQuery(id+"F0.imprint","IMPRINT",FACE,{"disambiguationData":[TD([[makeQuery(id+"F0.imprint","IMPRINT",EDGE,{"derivedFrom":sQuery(id+"F0.wireOp",EDGE,"E4")}),-1.0]])]});
            extrude(context, id + "F3", {"entities" : qUnion([Q0, Q1]), "operationType" : NewBodyOperationType.ADD, "oppositeDirection" : true, "depth" : 1.5 * mm});
        }
        {
            var Q0;
            Q0=makeQuery(id+"F1.opExtrude","CAP_FACE",FACE,{"disambiguationData":[OSD([sQuery(id+"F0.wireOp",EDGE,"E0.bottom"),sQuery(id+"F0.wireOp",EDGE,"E0.top"),sQuery(id+"F0.wireOp",EDGE,"E0.left"),sQuery(id+"F0.wireOp",EDGE,"E0.right"),sQuery(id+"F0.wireOp",EDGE,"E1"),sQuery(id+"F0.wireOp",EDGE,"E2"),sQuery(id+"F0.wireOp",EDGE,"E3")])],"isStart":false});
            var sketch = newSketch(context, id + "F4", { "sketchPlane" : qUnion([Q0])});
            skLineSegment(sketch, "E16.bottom", {"start": v(-10.16, 6.35) * mm, "end": v(-27.94, 6.35) * mm});
            skLineSegment(sketch, "E16.top", {"start": v(-10.16, 1.27) * mm, "end": v(-27.94, 1.27) * mm});
            skLineSegment(sketch, "E16.left", {"start": v(-10.16, 6.35) * mm, "end": v(-10.16, 1.27) * mm});
            skLineSegment(sketch, "E16.right", {"start": v(-27.94, 6.35) * mm, "end": v(-27.94, 1.27) * mm});
            skPoint(sketch, "E16.middle", {"position": v(-19.05, 3.8) * mm});
            skLineSegment(sketch, "E17.bottom", {"start": v(-10.16, 0.63) * mm, "end": v(-27.94, 0.63) * mm});
            skLineSegment(sketch, "E17.top", {"start": v(-10.16, -4.45) * mm, "end": v(-27.94, -4.45) * mm});
            skLineSegment(sketch, "E17.left", {"start": v(-10.16, 0.63) * mm, "end": v(-10.16, -4.45) * mm});
            skLineSegment(sketch, "E17.right", {"start": v(-27.94, 0.63) * mm, "end": v(-27.94, -4.44) * mm});
            skPoint(sketch, "E17.middle", {"position": v(-19.05, -1.9) * mm});
            skLineSegment(sketch, "E18.bottom", {"start": v(-12.06, -6.03) * mm, "end": v(-14.6, -6.03) * mm});
            skLineSegment(sketch, "E18.top", {"start": v(-12.06, -13.65) * mm, "end": v(-14.6, -13.65) * mm});
            skLineSegment(sketch, "E18.left", {"start": v(-12.06, -6.03) * mm, "end": v(-12.06, -13.65) * mm});
            skLineSegment(sketch, "E18.right", {"start": v(-14.6, -6.03) * mm, "end": v(-14.6, -13.65) * mm});
            skPoint(sketch, "E18.middle", {"position": v(-13.33, -9.84) * mm});
            skLineSegment(sketch, "E19.bottom", {"start": v(-8.89, -6.03) * mm, "end": v(-11.43, -6.03) * mm});
            skLineSegment(sketch, "E19.top", {"start": v(-8.89, -13.65) * mm, "end": v(-11.43, -13.65) * mm});
            skLineSegment(sketch, "E19.left", {"start": v(-8.89, -6.03) * mm, "end": v(-8.89, -13.65) * mm});
            skLineSegment(sketch, "E19.right", {"start": v(-11.43, -6.03) * mm, "end": v(-11.43, -13.65) * mm});
            skPoint(sketch, "E19.middle", {"position": v(-10.16, -9.84) * mm});
            skLineSegment(sketch, "E20.bottom", {"start": v(-5.71, -6.03) * mm, "end": v(-8.25, -6.03) * mm});
            skLineSegment(sketch, "E20.top", {"start": v(-5.71, -13.65) * mm, "end": v(-8.25, -13.65) * mm});
            skLineSegment(sketch, "E20.left", {"start": v(-5.71, -6.03) * mm, "end": v(-5.71, -13.65) * mm});
            skLineSegment(sketch, "E20.right", {"start": v(-8.25, -6.03) * mm, "end": v(-8.25, -13.65) * mm});
            skPoint(sketch, "E20.middle", {"position": v(-6.98, -9.84) * mm});
            skLineSegment(sketch, "E21.bottom", {"start": v(-2.54, -6.03) * mm, "end": v(-5.08, -6.03) * mm});
            skLineSegment(sketch, "E21.top", {"start": v(-2.54, -13.65) * mm, "end": v(-5.08, -13.65) * mm});
            skLineSegment(sketch, "E21.left", {"start": v(-2.54, -6.03) * mm, "end": v(-2.54, -13.65) * mm});
            skLineSegment(sketch, "E21.right", {"start": v(-5.08, -6.03) * mm, "end": v(-5.08, -13.65) * mm});
            skPoint(sketch, "E21.middle", {"position": v(-3.8, -9.84) * mm});
            skLineSegment(sketch, "E22.bottom", {"start": v(2.54, -8.57) * mm, "end": v(0, -8.57) * mm});
            skLineSegment(sketch, "E22.top", {"start": v(2.54, -13.65) * mm, "end": v(0, -13.65) * mm});
            skLineSegment(sketch, "E22.left", {"start": v(2.54, -8.57) * mm, "end": v(2.54, -13.65) * mm});
            skLineSegment(sketch, "E22.right", {"start": v(0, -8.57) * mm, "end": v(0, -13.65) * mm});
            skPoint(sketch, "E22.middle", {"position": v(1.27, -11.11) * mm});
            skLineSegment(sketch, "E23.bottom", {"start": v(5.72, -8.57) * mm, "end": v(3.18, -8.57) * mm});
            skLineSegment(sketch, "E23.top", {"start": v(5.72, -13.65) * mm, "end": v(3.18, -13.65) * mm});
            skLineSegment(sketch, "E23.left", {"start": v(5.72, -8.57) * mm, "end": v(5.72, -13.65) * mm});
            skLineSegment(sketch, "E23.right", {"start": v(3.18, -8.57) * mm, "end": v(3.18, -13.65) * mm});
            skPoint(sketch, "E23.middle", {"position": v(4.45, -11.11) * mm});
            skLineSegment(sketch, "E24.bottom", {"start": v(8.9, -8.57) * mm, "end": v(6.35, -8.57) * mm});
            skLineSegment(sketch, "E24.top", {"start": v(8.9, -13.65) * mm, "end": v(6.35, -13.65) * mm});
            skLineSegment(sketch, "E24.left", {"start": v(8.9, -8.57) * mm, "end": v(8.9, -13.65) * mm});
            skLineSegment(sketch, "E24.right", {"start": v(6.35, -8.57) * mm, "end": v(6.35, -13.65) * mm});
            skPoint(sketch, "E24.middle", {"position": v(7.62, -11.11) * mm});
            skLineSegment(sketch, "E25.bottom", {"start": v(12.07, -8.57) * mm, "end": v(9.53, -8.57) * mm});
            skLineSegment(sketch, "E25.top", {"start": v(12.07, -13.65) * mm, "end": v(9.53, -13.65) * mm});
            skLineSegment(sketch, "E25.left", {"start": v(12.07, -8.57) * mm, "end": v(12.07, -13.65) * mm});
            skLineSegment(sketch, "E25.right", {"start": v(9.53, -8.57) * mm, "end": v(9.53, -13.65) * mm});
            skPoint(sketch, "E25.middle", {"position": v(10.8, -11.11) * mm});
            skLineSegment(sketch, "E26.bottom", {"start": v(10.16, 4.45) * mm, "end": v(0, 4.45) * mm});
            skLineSegment(sketch, "E26.top", {"start": v(10.16, 6.99) * mm, "end": v(0, 6.99) * mm});
            skLineSegment(sketch, "E26.left", {"start": v(10.16, 4.45) * mm, "end": v(10.16, 6.99) * mm});
            skLineSegment(sketch, "E26.right", {"start": v(0, 4.45) * mm, "end": v(0, 6.99) * mm});
            skPoint(sketch, "E26.middle", {"position": v(5.08, 5.72) * mm});
            skLineSegment(sketch, "E27.bottom", {"start": v(10.16, 1.27) * mm, "end": v(0, 1.27) * mm});
            skLineSegment(sketch, "E27.top", {"start": v(10.16, 3.81) * mm, "end": v(0, 3.81) * mm});
            skLineSegment(sketch, "E27.left", {"start": v(10.16, 1.27) * mm, "end": v(10.16, 3.81) * mm});
            skLineSegment(sketch, "E27.right", {"start": v(0, 1.27) * mm, "end": v(0, 3.81) * mm});
            skPoint(sketch, "E27.middle", {"position": v(5.08, 2.54) * mm});
            skLineSegment(sketch, "E28.bottom", {"start": v(10.16, -1.9) * mm, "end": v(0, -1.9) * mm});
            skLineSegment(sketch, "E28.top", {"start": v(10.16, 0.64) * mm, "end": v(0, 0.64) * mm});
            skLineSegment(sketch, "E28.left", {"start": v(10.16, -1.9) * mm, "end": v(10.16, 0.64) * mm});
            skLineSegment(sketch, "E28.right", {"start": v(0, -1.9) * mm, "end": v(0, 0.64) * mm});
            skPoint(sketch, "E28.middle", {"position": v(5.08, -0.63) * mm});
            skLineSegment(sketch, "E29.bottom", {"start": v(10.16, -5.08) * mm, "end": v(0, -5.08) * mm});
            skLineSegment(sketch, "E29.top", {"start": v(10.16, -2.54) * mm, "end": v(0, -2.54) * mm});
            skLineSegment(sketch, "E29.left", {"start": v(10.16, -5.08) * mm, "end": v(10.16, -2.54) * mm});
            skLineSegment(sketch, "E29.right", {"start": v(0, -5.08) * mm, "end": v(0, -2.54) * mm});
            skPoint(sketch, "E29.middle", {"position": v(5.08, -3.8) * mm});
            skLineSegment(sketch, "E30.bottom", {"start": v(22.86, 5.72) * mm, "end": v(15.24, 5.72) * mm});
            skLineSegment(sketch, "E30.top", {"start": v(22.86, 8.26) * mm, "end": v(15.24, 8.26) * mm});
            skLineSegment(sketch, "E30.left", {"start": v(22.86, 5.72) * mm, "end": v(22.86, 8.26) * mm});
            skLineSegment(sketch, "E30.right", {"start": v(15.24, 5.72) * mm, "end": v(15.24, 8.26) * mm});
            skPoint(sketch, "E30.middle", {"position": v(19.05, 6.99) * mm});
            skLineSegment(sketch, "E31.bottom", {"start": v(22.86, 2.54) * mm, "end": v(15.24, 2.54) * mm});
            skLineSegment(sketch, "E31.top", {"start": v(22.86, 5.08) * mm, "end": v(15.24, 5.08) * mm});
            skLineSegment(sketch, "E31.left", {"start": v(22.86, 2.54) * mm, "end": v(22.86, 5.08) * mm});
            skLineSegment(sketch, "E31.right", {"start": v(15.24, 2.54) * mm, "end": v(15.24, 5.08) * mm});
            skPoint(sketch, "E31.middle", {"position": v(19.05, 3.81) * mm});
            skLineSegment(sketch, "E32.bottom", {"start": v(22.86, -0.63) * mm, "end": v(15.24, -0.63) * mm});
            skLineSegment(sketch, "E32.top", {"start": v(22.86, 1.9) * mm, "end": v(15.24, 1.9) * mm});
            skLineSegment(sketch, "E32.left", {"start": v(22.86, -0.63) * mm, "end": v(22.86, 1.9) * mm});
            skLineSegment(sketch, "E32.right", {"start": v(15.24, -0.63) * mm, "end": v(15.24, 1.9) * mm});
            skPoint(sketch, "E32.middle", {"position": v(19.05, 0.64) * mm});
            skLineSegment(sketch, "E33.bottom", {"start": v(22.86, -3.81) * mm, "end": v(15.24, -3.81) * mm});
            skLineSegment(sketch, "E33.top", {"start": v(22.86, -1.27) * mm, "end": v(15.24, -1.27) * mm});
            skLineSegment(sketch, "E33.left", {"start": v(22.86, -3.81) * mm, "end": v(22.86, -1.27) * mm});
            skLineSegment(sketch, "E33.right", {"start": v(15.24, -3.81) * mm, "end": v(15.24, -1.27) * mm});
            skPoint(sketch, "E33.middle", {"position": v(19.05, -2.54) * mm});
            skLineSegment(sketch, "E34.bottom", {"start": v(22.86, -6.98) * mm, "end": v(15.24, -6.98) * mm});
            skLineSegment(sketch, "E34.top", {"start": v(22.86, -4.44) * mm, "end": v(15.24, -4.44) * mm});
            skLineSegment(sketch, "E34.left", {"start": v(22.86, -6.98) * mm, "end": v(22.86, -4.44) * mm});
            skLineSegment(sketch, "E34.right", {"start": v(15.24, -6.98) * mm, "end": v(15.24, -4.44) * mm});
            skPoint(sketch, "E34.middle", {"position": v(19.05, -5.71) * mm});
            skLineSegment(sketch, "E35.bottom", {"start": v(22.86, -10.16) * mm, "end": v(15.24, -10.16) * mm});
            skLineSegment(sketch, "E35.top", {"start": v(22.86, -7.62) * mm, "end": v(15.24, -7.62) * mm});
            skLineSegment(sketch, "E35.left", {"start": v(22.86, -10.16) * mm, "end": v(22.86, -7.62) * mm});
            skLineSegment(sketch, "E35.right", {"start": v(15.24, -10.16) * mm, "end": v(15.24, -7.62) * mm});
            skPoint(sketch, "E35.middle", {"position": v(19.05, -8.89) * mm});
            skLineSegment(sketch, "E36.bottom", {"start": v(22.86, -13.34) * mm, "end": v(15.24, -13.34) * mm});
            skLineSegment(sketch, "E36.top", {"start": v(22.86, -10.8) * mm, "end": v(15.24, -10.8) * mm});
            skLineSegment(sketch, "E36.left", {"start": v(22.86, -13.34) * mm, "end": v(22.86, -10.8) * mm});
            skLineSegment(sketch, "E36.right", {"start": v(15.24, -13.34) * mm, "end": v(15.24, -10.8) * mm});
            skPoint(sketch, "E36.middle", {"position": v(19.05, -12.07) * mm});
            skLineSegment(sketch, "E37", {"start": v(-13.33, -9.84) * mm, "end": v(-10.16, -9.84) * mm, "construction": true});
            skLineSegment(sketch, "E38", {"start": v(-10.16, -9.84) * mm, "end": v(-6.98, -9.84) * mm, "construction": true});
            skLineSegment(sketch, "E39", {"start": v(-6.98, -9.84) * mm, "end": v(-3.8, -9.84) * mm, "construction": true});
            skLineSegment(sketch, "E40", {"start": v(1.27, -11.11) * mm, "end": v(4.45, -11.11) * mm, "construction": true});
            skLineSegment(sketch, "E41", {"start": v(4.45, -11.11) * mm, "end": v(7.62, -11.11) * mm, "construction": true});
            skLineSegment(sketch, "E42", {"start": v(7.62, -11.11) * mm, "end": v(10.8, -11.11) * mm, "construction": true});
            skLineSegment(sketch, "E43", {"start": v(5.08, -3.8) * mm, "end": v(5.08, -0.63) * mm, "construction": true});
            skLineSegment(sketch, "E44", {"start": v(5.08, -0.63) * mm, "end": v(5.08, 2.54) * mm, "construction": true});
            skLineSegment(sketch, "E45", {"start": v(5.08, 2.54) * mm, "end": v(5.08, 5.72) * mm, "construction": true});
            skLineSegment(sketch, "E46", {"start": v(19.05, 6.99) * mm, "end": v(19.05, 3.81) * mm, "construction": true});
            skLineSegment(sketch, "E47", {"start": v(19.05, 3.81) * mm, "end": v(19.05, 0.64) * mm, "construction": true});
            skLineSegment(sketch, "E48", {"start": v(19.05, 0.64) * mm, "end": v(19.05, -2.54) * mm, "construction": true});
            skLineSegment(sketch, "E49", {"start": v(19.05, -2.54) * mm, "end": v(19.05, -5.71) * mm, "construction": true});
            skLineSegment(sketch, "E50", {"start": v(19.05, -5.71) * mm, "end": v(19.05, -8.89) * mm, "construction": true});
            skLineSegment(sketch, "E51", {"start": v(19.05, -8.89) * mm, "end": v(19.05, -12.07) * mm, "construction": true});
            skSolve(sketch);
        }
        {
            var Q0;
            Q0=makeQuery(id+"F4.imprint","IMPRINT",FACE,{"disambiguationData":[TD([[makeQuery(id+"F4.imprint","IMPRINT",EDGE,{"derivedFrom":sQuery(id+"F4.wireOp",EDGE,"E16.bottom")}),1.0]])]});
            var Q1;
            Q1=makeQuery(id+"F4.imprint","IMPRINT",FACE,{"disambiguationData":[TD([[makeQuery(id+"F4.imprint","IMPRINT",EDGE,{"derivedFrom":sQuery(id+"F4.wireOp",EDGE,"E17.bottom")}),1.0]])]});
            var Q2;
            Q2=makeQuery(id+"F4.imprint","IMPRINT",FACE,{"disambiguationData":[TD([[makeQuery(id+"F4.imprint","IMPRINT",EDGE,{"derivedFrom":sQuery(id+"F4.wireOp",EDGE,"E18.bottom")}),1.0]])]});
            var Q3;
            Q3=makeQuery(id+"F4.imprint","IMPRINT",FACE,{"disambiguationData":[TD([[makeQuery(id+"F4.imprint","IMPRINT",EDGE,{"derivedFrom":sQuery(id+"F4.wireOp",EDGE,"E19.bottom")}),1.0]])]});
            var Q4;
            Q4=makeQuery(id+"F4.imprint","IMPRINT",FACE,{"disambiguationData":[TD([[makeQuery(id+"F4.imprint","IMPRINT",EDGE,{"derivedFrom":sQuery(id+"F4.wireOp",EDGE,"E20.bottom")}),1.0]])]});
            var Q5;
            Q5=makeQuery(id+"F4.imprint","IMPRINT",FACE,{"disambiguationData":[TD([[makeQuery(id+"F4.imprint","IMPRINT",EDGE,{"derivedFrom":sQuery(id+"F4.wireOp",EDGE,"E21.bottom")}),1.0]])]});
            var Q6;
            Q6=makeQuery(id+"F4.imprint","IMPRINT",FACE,{"disambiguationData":[TD([[makeQuery(id+"F4.imprint","IMPRINT",EDGE,{"derivedFrom":sQuery(id+"F4.wireOp",EDGE,"E22.bottom")}),1.0]])]});
            var Q7;
            Q7=makeQuery(id+"F4.imprint","IMPRINT",FACE,{"disambiguationData":[TD([[makeQuery(id+"F4.imprint","IMPRINT",EDGE,{"derivedFrom":sQuery(id+"F4.wireOp",EDGE,"E23.bottom")}),1.0]])]});
            var Q8;
            Q8=makeQuery(id+"F4.imprint","IMPRINT",FACE,{"disambiguationData":[TD([[makeQuery(id+"F4.imprint","IMPRINT",EDGE,{"derivedFrom":sQuery(id+"F4.wireOp",EDGE,"E24.bottom")}),1.0]])]});
            var Q9;
            Q9=makeQuery(id+"F4.imprint","IMPRINT",FACE,{"disambiguationData":[TD([[makeQuery(id+"F4.imprint","IMPRINT",EDGE,{"derivedFrom":sQuery(id+"F4.wireOp",EDGE,"E25.bottom")}),1.0]])]});
            var Q10;
            Q10=makeQuery(id+"F4.imprint","IMPRINT",FACE,{"disambiguationData":[TD([[makeQuery(id+"F4.imprint","IMPRINT",EDGE,{"derivedFrom":sQuery(id+"F4.wireOp",EDGE,"E29.bottom")}),-1.0]])]});
            var Q11;
            Q11=makeQuery(id+"F4.imprint","IMPRINT",FACE,{"disambiguationData":[TD([[makeQuery(id+"F4.imprint","IMPRINT",EDGE,{"derivedFrom":sQuery(id+"F4.wireOp",EDGE,"E28.bottom")}),-1.0]])]});
            var Q12;
            Q12=makeQuery(id+"F4.imprint","IMPRINT",FACE,{"disambiguationData":[TD([[makeQuery(id+"F4.imprint","IMPRINT",EDGE,{"derivedFrom":sQuery(id+"F4.wireOp",EDGE,"E27.bottom")}),-1.0]])]});
            var Q13;
            Q13=makeQuery(id+"F4.imprint","IMPRINT",FACE,{"disambiguationData":[TD([[makeQuery(id+"F4.imprint","IMPRINT",EDGE,{"derivedFrom":sQuery(id+"F4.wireOp",EDGE,"E26.bottom")}),-1.0]])]});
            var Q14;
            Q14=makeQuery(id+"F4.imprint","IMPRINT",FACE,{"disambiguationData":[TD([[makeQuery(id+"F4.imprint","IMPRINT",EDGE,{"derivedFrom":sQuery(id+"F4.wireOp",EDGE,"E30.bottom")}),-1.0]])]});
            var Q15;
            Q15=makeQuery(id+"F4.imprint","IMPRINT",FACE,{"disambiguationData":[TD([[makeQuery(id+"F4.imprint","IMPRINT",EDGE,{"derivedFrom":sQuery(id+"F4.wireOp",EDGE,"E31.bottom")}),-1.0]])]});
            var Q16;
            Q16=makeQuery(id+"F4.imprint","IMPRINT",FACE,{"disambiguationData":[TD([[makeQuery(id+"F4.imprint","IMPRINT",EDGE,{"derivedFrom":sQuery(id+"F4.wireOp",EDGE,"E32.bottom")}),-1.0]])]});
            var Q17;
            Q17=makeQuery(id+"F4.imprint","IMPRINT",FACE,{"disambiguationData":[TD([[makeQuery(id+"F4.imprint","IMPRINT",EDGE,{"derivedFrom":sQuery(id+"F4.wireOp",EDGE,"E33.bottom")}),-1.0]])]});
            var Q18;
            Q18=makeQuery(id+"F4.imprint","IMPRINT",FACE,{"disambiguationData":[TD([[makeQuery(id+"F4.imprint","IMPRINT",EDGE,{"derivedFrom":sQuery(id+"F4.wireOp",EDGE,"E34.bottom")}),-1.0]])]});
            var Q19;
            Q19=makeQuery(id+"F4.imprint","IMPRINT",FACE,{"disambiguationData":[TD([[makeQuery(id+"F4.imprint","IMPRINT",EDGE,{"derivedFrom":sQuery(id+"F4.wireOp",EDGE,"E35.bottom")}),-1.0]])]});
            var Q20;
            Q20=makeQuery(id+"F4.imprint","IMPRINT",FACE,{"disambiguationData":[TD([[makeQuery(id+"F4.imprint","IMPRINT",EDGE,{"derivedFrom":sQuery(id+"F4.wireOp",EDGE,"E36.bottom")}),-1.0]])]});
            extrude(context, id + "F5", {"entities" : qUnion([Q0, Q1, Q2, Q3, Q4, Q5, Q6, Q7, Q8, Q9, Q10, Q11, Q12, Q13, Q14, Q15, Q16, Q17, Q18, Q19, Q20]), "operationType" : NewBodyOperationType.ADD, "depth" : 8.25 * mm});
        }
    });
